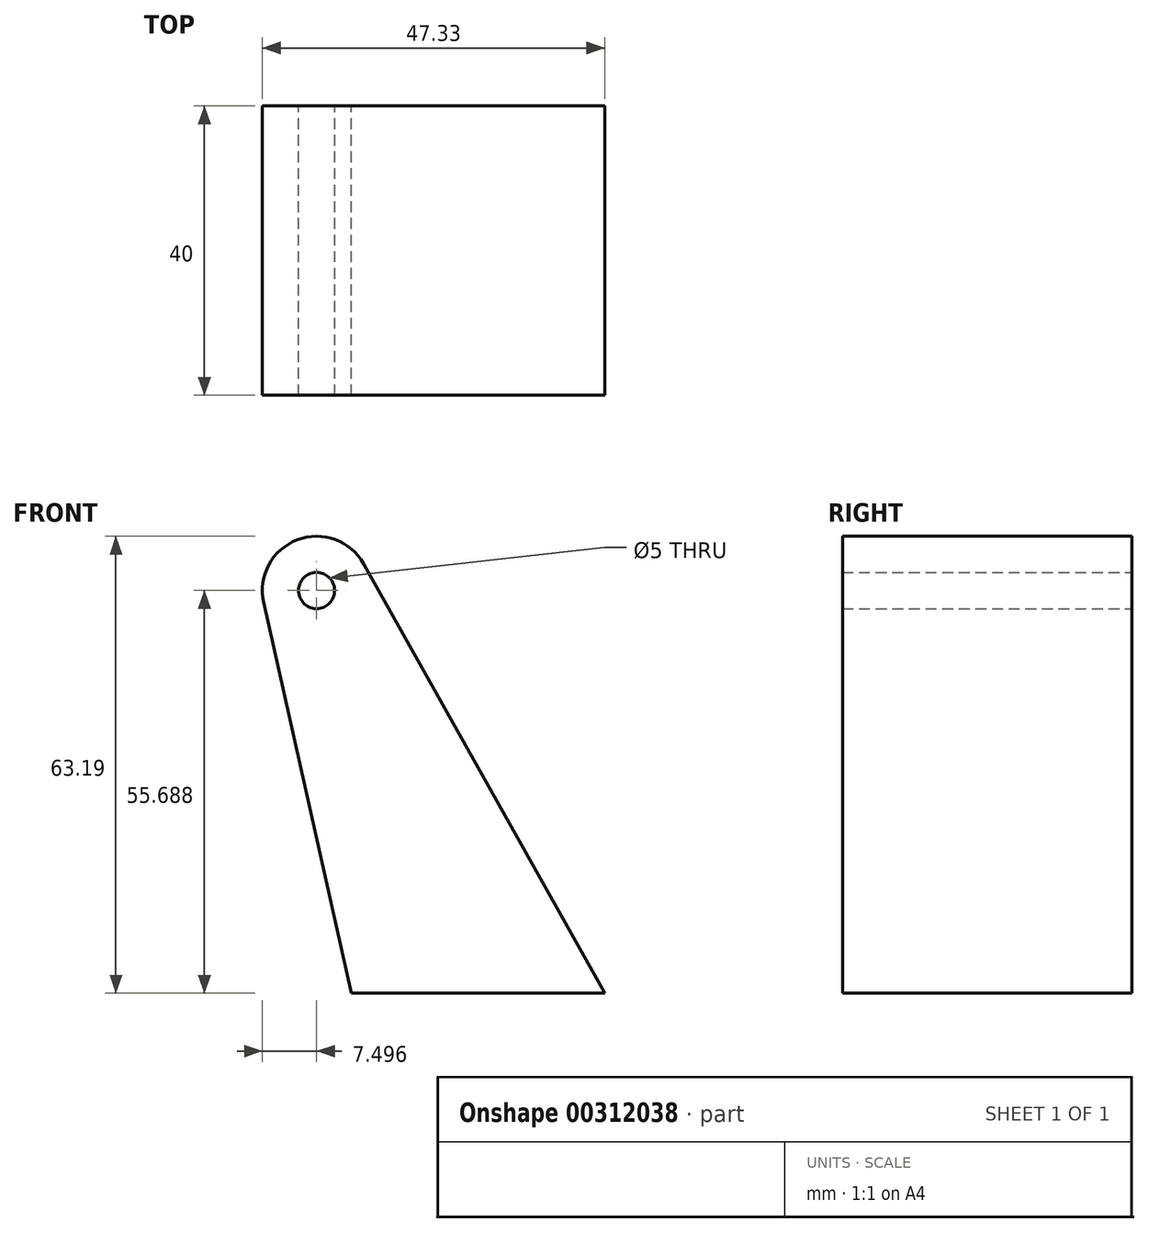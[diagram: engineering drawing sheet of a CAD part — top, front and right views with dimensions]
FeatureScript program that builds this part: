
annotation { "Feature Type Name" : "Feature", "Feature Type Description" : "" }
export const myFeature = defineFeature(function(context is Context, id is Id, definition is map)
    precondition{}
    {
        {
            var Q0;
            Q0=qCreatedBy(makeId("Front.planeOp"),FACE);
            var sketch = newSketch(context, id + "F0", { "sketchPlane" : qUnion([Q0])});
            skLineSegment(sketch, "E0", {"start": v(-17.5, 0) * mm, "end": v(17.5, 0) * mm});
            skCircle(sketch, "E1", {"center": v(-22.33, 55.69) * mm, "radius": 7.5 * mm});
            skLineSegment(sketch, "E2", {"start": v(17.5, 0) * mm, "end": v(-15.8, 59.36) * mm});
            skLineSegment(sketch, "E3", {"start": v(-17.5, 0) * mm, "end": v(-29.65, 54.04) * mm});
            skLineSegment(sketch, "E4", {"start": v(0, 0) * mm, "end": v(-22.33, 55.69) * mm});
            skCircle(sketch, "E5", {"center": v(-22.33, 55.69) * mm, "radius": 2.5 * mm});
            skSolve(sketch);
        }
        {
            var Q0;
            Q0 = qSketchRegion(id + "F0", true);
            extrude(context, id + "F1", {"entities" : qUnion([Q0]), "depth" : 40 * mm});
        }
    });
